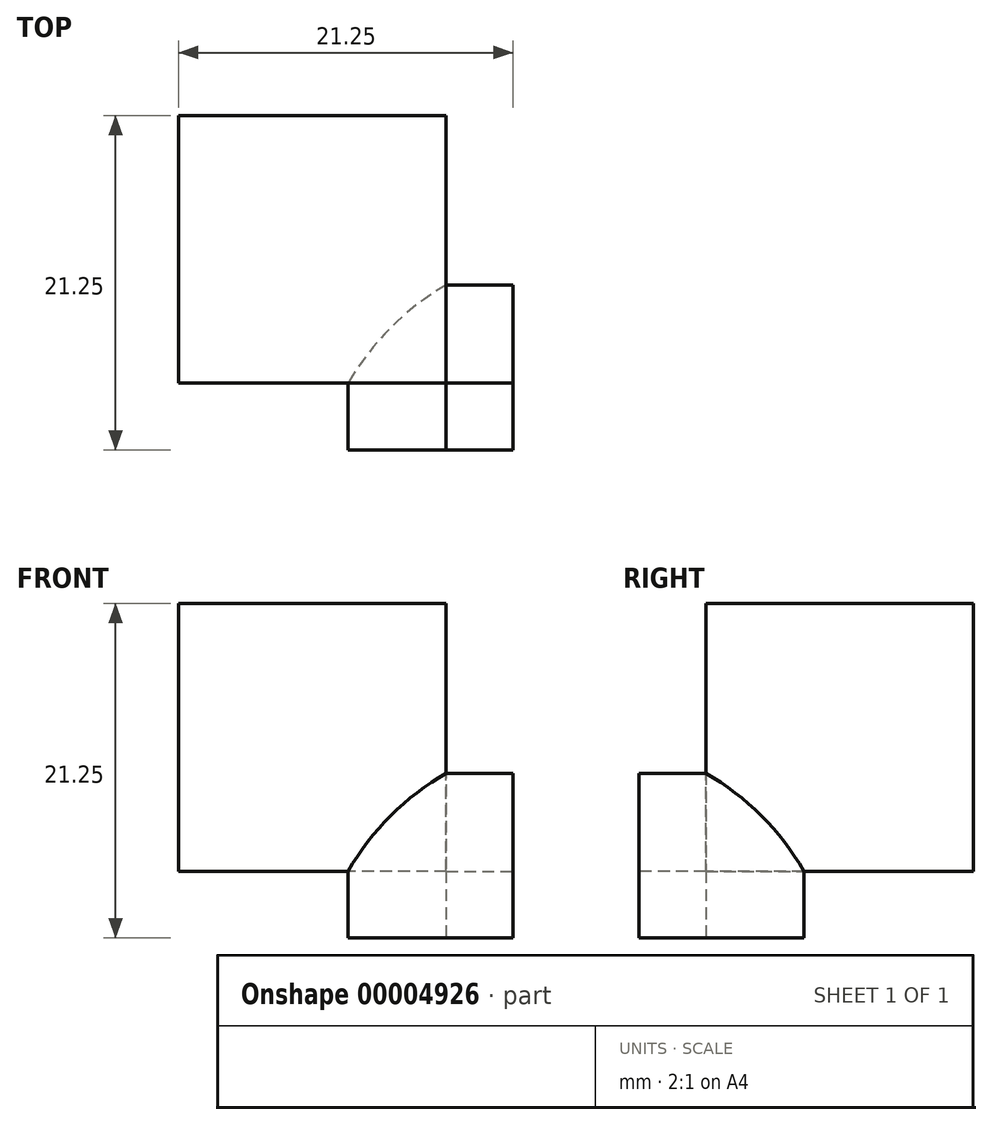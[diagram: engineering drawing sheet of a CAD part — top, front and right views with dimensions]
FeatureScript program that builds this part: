
annotation { "Feature Type Name" : "Feature", "Feature Type Description" : "" }
export const myFeature = defineFeature(function(context is Context, id is Id, definition is map)
    precondition{}
    {
        {
            var Q0;
            Q0=qCreatedBy(makeId("Top.planeOp"),FACE);
            var sketch = newSketch(context, id + "F0", { "sketchPlane" : qUnion([Q0])});
            skLineSegment(sketch, "E0", {"start": v(0, 4.25) * mm, "end": v(8.5, 4.25) * mm, "construction": true});
            skLineSegment(sketch, "E1", {"start": v(0, 4.25) * mm, "end": v(0, -12.75) * mm, "construction": true});
            skLineSegment(sketch, "E2", {"start": v(8.5, 4.25) * mm, "end": v(8.5, -12.75) * mm, "construction": true});
            skLineSegment(sketch, "E3", {"start": v(0, -12.75) * mm, "end": v(8.5, -12.75) * mm, "construction": true});
            skLineSegment(sketch, "E4", {"start": v(4.25, 4.25) * mm, "end": v(4.25, -12.75) * mm, "construction": true});
            skLineSegment(sketch, "E5.rect.bottom", {"start": v(12.75, -8.5) * mm, "end": v(-4.25, -8.5) * mm, "construction": true});
            skLineSegment(sketch, "E5.rect.top", {"start": v(12.75, 0) * mm, "end": v(-4.25, 0) * mm, "construction": true});
            skLineSegment(sketch, "E5.rect.left", {"start": v(12.75, -8.5) * mm, "end": v(12.75, 0) * mm, "construction": true});
            skLineSegment(sketch, "E5.rect.right", {"start": v(-4.25, -8.5) * mm, "end": v(-4.25, 0) * mm, "construction": true});
            skPoint(sketch, "E5.rect.middle", {"position": v(4.25, -4.25) * mm});
            skCircle(sketch, "E6", {"center": v(4.25, -4.25) * mm, "radius": 17 * mm, "construction": true});
            skSolve(sketch);
        }
        {
            var Q0;
            Q0=qCreatedBy(makeId("Top.planeOp"),FACE);
            var sketch = newSketch(context, id + "F1", { "sketchPlane" : qUnion([Q0])});
            skLineSegment(sketch, "E7", {"start": v(0, 0) * mm, "end": v(-4.25, 0) * mm, "construction": true});
            skLineSegment(sketch, "E8", {"start": v(-4.25, 0) * mm, "end": v(-4.25, 4.25) * mm, "construction": true});
            skLineSegment(sketch, "E9.bottom", {"start": v(-4.25, 4.25) * mm, "end": v(-21.25, 4.25) * mm});
            skLineSegment(sketch, "E9.top", {"start": v(-4.25, 21.25) * mm, "end": v(-21.25, 21.25) * mm});
            skLineSegment(sketch, "E9.left", {"start": v(-4.25, 4.25) * mm, "end": v(-4.25, 21.25) * mm});
            skLineSegment(sketch, "E9.right", {"start": v(-21.25, 4.25) * mm, "end": v(-21.25, 21.25) * mm});
            skSolve(sketch);
        }
        {
            var Q0;
            Q0=qCreatedBy(makeId("Front.planeOp"),FACE);
            var sketch = newSketch(context, id + "F2", { "sketchPlane" : qUnion([Q0])});
            skLineSegment(sketch, "E10", {"start": v(-4.25, 0) * mm, "end": v(-4.25, 4.25) * mm, "construction": true});
            skLineSegment(sketch, "E11.bottom", {"start": v(-4.25, 4.25) * mm, "end": v(-21.25, 4.25) * mm});
            skLineSegment(sketch, "E11.top", {"start": v(-4.25, 21.25) * mm, "end": v(-21.25, 21.25) * mm});
            skLineSegment(sketch, "E11.left", {"start": v(-4.25, 4.25) * mm, "end": v(-4.25, 21.25) * mm});
            skLineSegment(sketch, "E11.right", {"start": v(-21.25, 4.25) * mm, "end": v(-21.25, 21.25) * mm});
            skSolve(sketch);
        }
        {
            var Q0;
            Q0=makeQuery(id+"F1.imprint","IMPRINT",FACE,{"disambiguationData":[TD([[makeQuery(id+"F1.imprint","IMPRINT",EDGE,{"derivedFrom":sQuery(id+"F1.wireOp",EDGE,"E9.bottom")}),-1.0]])]});
            extrude(context, id + "F3", {"entities" : qUnion([Q0]), "depth" : 21.25 * mm});
        }
        {
            var Q0;
            Q0 = qSketchRegion(id + "F1", true);
            extrude(context, id + "F4", {"entities" : qUnion([Q0]), "operationType" : NewBodyOperationType.REMOVE, "depth" : 4.25 * mm});
        }
        {
            var Q0;
            Q0 = qSketchRegion(id + "F2", true);
            extrude(context, id + "F5", {"entities" : qUnion([Q0]), "operationType" : NewBodyOperationType.ADD, "oppositeDirection" : true, "depth" : 21.25 * mm});
        }
        {
            var Q0;
            Q0 = qSketchRegion(id + "F2", true);
            extrude(context, id + "F6", {"entities" : qUnion([Q0]), "operationType" : NewBodyOperationType.REMOVE, "oppositeDirection" : true, "depth" : 4.25 * mm});
        }
        {
            var Q0;
            Q0=qCreatedBy(makeId("Top.planeOp"),FACE);
            var sketch = newSketch(context, id + "F7", { "sketchPlane" : qUnion([Q0])});
            skLineSegment(sketch, "E12.left", {"start": v(0, 0) * mm, "end": v(0, 0) * mm});
            skLineSegment(sketch, "E12.right", {"start": v(-4.25, 0) * mm, "end": v(-4.25, 0) * mm});
            skLineSegment(sketch, "E13.bottom", {"start": v(0, 0) * mm, "end": v(-4.25, 0) * mm});
            skLineSegment(sketch, "E13.top", {"start": v(0, 4.25) * mm, "end": v(-4.25, 4.25) * mm});
            skLineSegment(sketch, "E13.left", {"start": v(0, 0) * mm, "end": v(0, 4.25) * mm});
            skLineSegment(sketch, "E13.right", {"start": v(-4.25, 0) * mm, "end": v(-4.25, 4.25) * mm});
            skLineSegment(sketch, "E14", {"start": v(-4.25, 4.25) * mm, "end": v(-10.47, 4.25) * mm, "construction": true});
            skLineSegment(sketch, "E15", {"start": v(-4.25, 4.25) * mm, "end": v(-4.25, 10.47) * mm, "construction": true});
            skLineSegment(sketch, "E16", {"start": v(-10.47, 4.25) * mm, "end": v(-10.47, 0) * mm});
            skLineSegment(sketch, "E17", {"start": v(-10.47, 0) * mm, "end": v(-4.25, 0) * mm});
            skLineSegment(sketch, "E18", {"start": v(-4.25, 10.47) * mm, "end": v(0, 10.47) * mm});
            skLineSegment(sketch, "E19", {"start": v(0, 10.47) * mm, "end": v(0, 4.25) * mm});
            skArc(sketch, "E20", {"start": v(-4.25, 10.47) * mm, "mid": v(-7.77, 7.77) * mm, "end": v(-10.47, 4.25) * mm});
            skArc(sketch, "E21", {"start": v(-10.47, 4.25) * mm, "mid": v(16.27, -16.27) * mm, "end": v(-4.25, 10.47) * mm, "construction": true});
            skLineSegment(sketch, "E22", {"start": v(-10.47, 4.25) * mm, "end": v(-10.47, 10.47) * mm});
            skLineSegment(sketch, "E23", {"start": v(-4.25, 10.47) * mm, "end": v(-10.47, 10.47) * mm});
            skSolve(sketch);
        }
        {
            var Q0;
            Q0=qCreatedBy(makeId("Front.planeOp"),FACE);
            var sketch = newSketch(context, id + "F8", { "sketchPlane" : qUnion([Q0])});
            skLineSegment(sketch, "E24.bottom", {"start": v(0, 0) * mm, "end": v(-4.25, 0) * mm});
            skLineSegment(sketch, "E24.top", {"start": v(0, 4.25) * mm, "end": v(-4.25, 4.25) * mm});
            skLineSegment(sketch, "E24.left", {"start": v(0, 0) * mm, "end": v(0, 4.25) * mm});
            skLineSegment(sketch, "E24.right", {"start": v(-4.25, 0) * mm, "end": v(-4.25, 4.25) * mm});
            skLineSegment(sketch, "E25", {"start": v(-4.25, 0) * mm, "end": v(0, 4.25) * mm, "construction": true});
            skPoint(sketch, "E26", {"position": v(0, 4.25) * mm});
            skLineSegment(sketch, "E27", {"start": v(4.25, 0) * mm, "end": v(4.25, -4.25) * mm, "construction": true});
            skLineSegment(sketch, "E28", {"start": v(-4.25, 4.25) * mm, "end": v(-10.47, 4.25) * mm, "construction": true});
            skLineSegment(sketch, "E29", {"start": v(-4.25, 4.25) * mm, "end": v(-4.25, 10.47) * mm, "construction": true});
            skLineSegment(sketch, "E30", {"start": v(-4.25, 10.47) * mm, "end": v(0, 10.47) * mm});
            skLineSegment(sketch, "E31", {"start": v(0, 10.47) * mm, "end": v(0, 4.25) * mm});
            skLineSegment(sketch, "E32", {"start": v(-10.47, 4.25) * mm, "end": v(-10.47, 0) * mm});
            skLineSegment(sketch, "E33", {"start": v(-10.47, 0) * mm, "end": v(-4.25, 0) * mm});
            skArc(sketch, "E34", {"start": v(-4.25, 10.47) * mm, "mid": v(-7.77, 7.77) * mm, "end": v(-10.47, 4.25) * mm});
            skArc(sketch, "E35", {"start": v(-10.47, 4.25) * mm, "mid": v(16.27, -16.27) * mm, "end": v(-4.25, 10.47) * mm, "construction": true});
            skLineSegment(sketch, "E36", {"start": v(-10.47, 4.25) * mm, "end": v(-10.47, 10.47) * mm});
            skLineSegment(sketch, "E37", {"start": v(-4.25, 10.47) * mm, "end": v(-10.47, 10.47) * mm});
            skSolve(sketch);
        }
        {
            var Q0;
            Q0=qCreatedBy(makeId("Right.planeOp"),FACE);
            var sketch = newSketch(context, id + "F9", { "sketchPlane" : qUnion([Q0])});
            skLineSegment(sketch, "E38.bottom", {"start": v(0, 0) * mm, "end": v(0, 0) * mm});
            skLineSegment(sketch, "E38.top", {"start": v(0, 4.25) * mm, "end": v(0, 4.25) * mm});
            skLineSegment(sketch, "E39.bottom", {"start": v(0, 0) * mm, "end": v(4.25, 0) * mm});
            skLineSegment(sketch, "E39.top", {"start": v(0, 4.25) * mm, "end": v(4.25, 4.25) * mm});
            skLineSegment(sketch, "E39.left", {"start": v(0, 0) * mm, "end": v(0, 4.25) * mm});
            skLineSegment(sketch, "E39.right", {"start": v(4.25, 0) * mm, "end": v(4.25, 4.25) * mm});
            skLineSegment(sketch, "E40", {"start": v(-4.25, 0) * mm, "end": v(-4.25, -4.25) * mm, "construction": true});
            skLineSegment(sketch, "E41", {"start": v(4.25, 4.25) * mm, "end": v(4.25, 10.47) * mm, "construction": true});
            skLineSegment(sketch, "E42", {"start": v(4.25, 4.25) * mm, "end": v(10.47, 4.25) * mm, "construction": true});
            skLineSegment(sketch, "E43", {"start": v(10.47, 4.25) * mm, "end": v(10.47, 0) * mm});
            skLineSegment(sketch, "E44", {"start": v(10.47, 0) * mm, "end": v(4.25, 0) * mm});
            skLineSegment(sketch, "E45", {"start": v(4.25, 10.47) * mm, "end": v(0, 10.47) * mm});
            skLineSegment(sketch, "E46", {"start": v(0, 10.47) * mm, "end": v(0, 4.25) * mm});
            skArc(sketch, "E47", {"start": v(4.25, 10.47) * mm, "mid": v(-16.27, -16.27) * mm, "end": v(10.47, 4.25) * mm, "construction": true});
            skArc(sketch, "E48", {"start": v(10.47, 4.25) * mm, "mid": v(7.77, 7.77) * mm, "end": v(4.25, 10.47) * mm});
            skLineSegment(sketch, "E49", {"start": v(10.47, 4.25) * mm, "end": v(10.47, 10.47) * mm});
            skLineSegment(sketch, "E50", {"start": v(4.25, 10.47) * mm, "end": v(10.47, 10.47) * mm});
            skSolve(sketch);
        }
        {
            var Q0;
            Q0 = qSketchRegion(id + "F7", true);
            extrude(context, id + "F10", {"entities" : qUnion([Q0]), "depth" : 7.8 * mm});
        }
        {
            var Q0;
            Q0 = qSketchRegion(id + "F8", true);
            var Q1;
            Q1=makeQuery(id+"F10.opExtrude","SWEPT_FACE",FACE,{"disambiguationData":[OSD([sQuery(id+"F7.wireOp",EDGE,"E18")])]});
            extrude(context, id + "F11", {"entities" : qUnion([Q0]), "operationType" : NewBodyOperationType.ADD, "endBound" : BoundingType.UP_TO_SURFACE, "oppositeDirection" : true, "endBoundEntityFace" : qUnion([Q1]), "depth" : 8.5 * mm});
        }
        {
            var Q0;
            Q0 = qSketchRegion(id + "F9", true);
            var Q1;
            Q1=makeQuery(id+"F10.opExtrude","SWEPT_FACE",FACE,{"disambiguationData":[OSD([sQuery(id+"F7.wireOp",EDGE,"E16"),sQuery(id+"F7.wireOp",EDGE,"E22")])]});
            extrude(context, id + "F12", {"entities" : qUnion([Q0]), "operationType" : NewBodyOperationType.ADD, "endBound" : BoundingType.UP_TO_SURFACE, "oppositeDirection" : true, "endBoundEntityFace" : qUnion([Q1]), "depth" : 8.5 * mm});
        }
        {
            var Q0;
            Q0=makeQuery(id+"F7.imprint","IMPRINT",FACE,{"disambiguationData":[TD([[makeQuery(id+"F7.imprint","IMPRINT",EDGE,{"derivedFrom":sQuery(id+"F7.wireOp",EDGE,"E13.bottom")}),-1.0]])]});
            var Q1;
            Q1=makeQuery(id+"F7.imprint","IMPRINT",FACE,{"disambiguationData":[TD([[makeQuery(id+"F7.imprint","IMPRINT",EDGE,{"derivedFrom":sQuery(id+"F7.wireOp",EDGE,"E13.top")}),-1.0]])]});
            var Q2;
            Q2=makeQuery(id+"F12.boolean.opBoolean","MERGE",FACE,{"derivedFrom":[makeQuery(id+"F11.opExtrude","SWEPT_FACE",FACE,{"disambiguationData":[OSD([sQuery(id+"F8.wireOp",EDGE,"E30")])]}),makeQuery(id+"F12.opExtrude","SWEPT_FACE",FACE,{"disambiguationData":[OSD([sQuery(id+"F9.wireOp",EDGE,"E45")])]})]});
            extrude(context, id + "F13", {"entities" : qUnion([Q0, Q1]), "operationType" : NewBodyOperationType.ADD, "endBound" : BoundingType.UP_TO_SURFACE, "endBoundEntityFace" : qUnion([Q2]), "depth" : 4.98 * mm});
        }
        {
            var Q0;
            Q0=makeQuery(id+"F7.imprint","IMPRINT",FACE,{"disambiguationData":[TD([[makeQuery(id+"F7.imprint","IMPRINT",EDGE,{"derivedFrom":sQuery(id+"F7.wireOp",EDGE,"E20")}),-1.0]])]});
            extrude(context, id + "F14", {"entities" : qUnion([Q0]), "operationType" : NewBodyOperationType.REMOVE, "depth" : 4.25 * mm});
        }
        {
            var Q0;
            Q0=makeQuery(id+"F8.imprint","IMPRINT",FACE,{"disambiguationData":[TD([[makeQuery(id+"F8.imprint","IMPRINT",EDGE,{"derivedFrom":sQuery(id+"F8.wireOp",EDGE,"E34")}),-1.0]])]});
            extrude(context, id + "F15", {"entities" : qUnion([Q0]), "operationType" : NewBodyOperationType.REMOVE, "oppositeDirection" : true, "depth" : 4.25 * mm});
        }
        {
            var Q0;
            Q0=makeQuery(id+"F9.imprint","IMPRINT",FACE,{"disambiguationData":[TD([[makeQuery(id+"F9.imprint","IMPRINT",EDGE,{"derivedFrom":sQuery(id+"F9.wireOp",EDGE,"E48")}),-1.0]])]});
            extrude(context, id + "F16", {"entities" : qUnion([Q0]), "operationType" : NewBodyOperationType.REMOVE, "oppositeDirection" : true, "depth" : 4.25 * mm});
        }
    });
